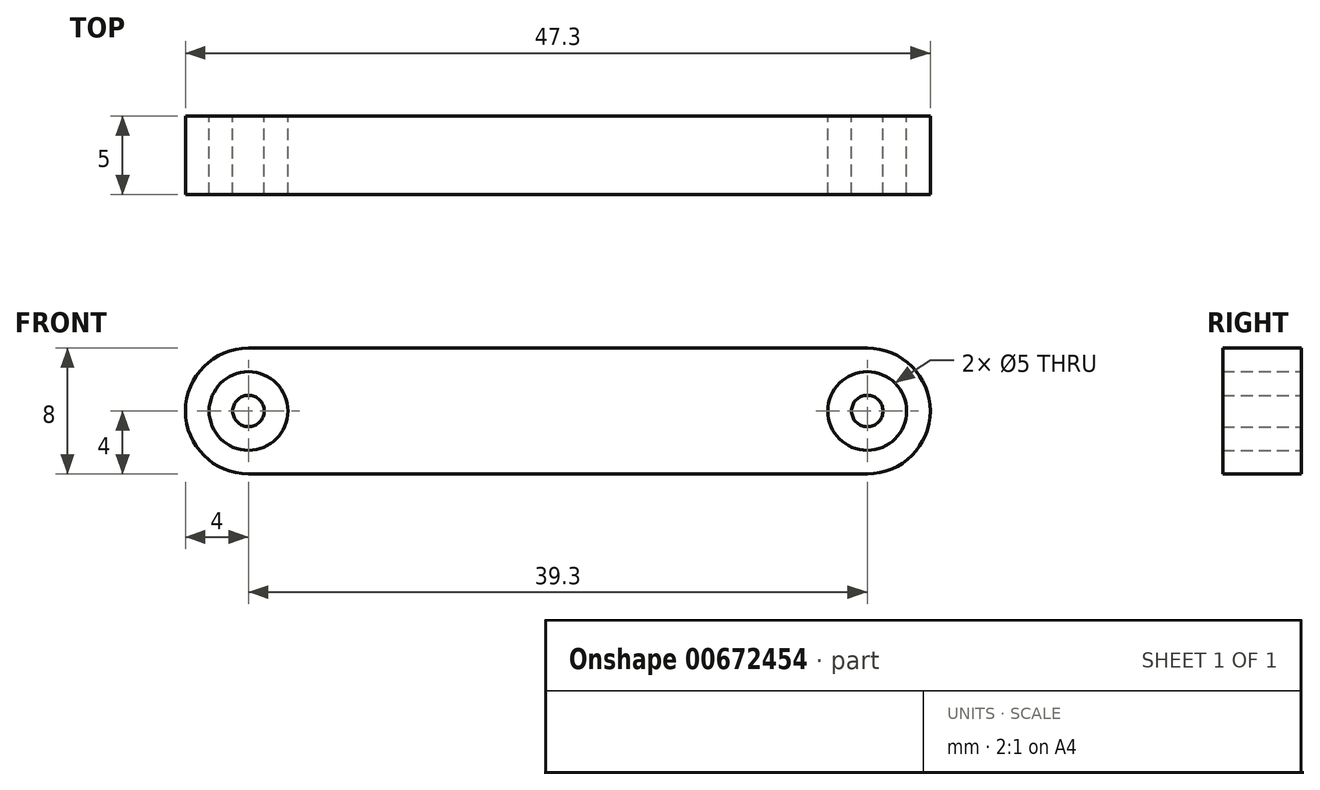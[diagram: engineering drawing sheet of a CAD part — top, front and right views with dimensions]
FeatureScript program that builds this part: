
annotation { "Feature Type Name" : "Feature", "Feature Type Description" : "" }
export const myFeature = defineFeature(function(context is Context, id is Id, definition is map)
    precondition{}
    {
        {
            var Q0;
            Q0=qCreatedBy(makeId("Front.planeOp"),FACE);
            var sketch = newSketch(context, id + "F0", { "sketchPlane" : qUnion([Q0])});
            skArc(sketch, "E0", {"start": v(0, 4) * mm, "mid": v(-4, 0) * mm, "end": v(0, -4) * mm});
            skCircle(sketch, "E1", {"center": v(0, 0) * mm, "radius": 2.5 * mm});
            skArc(sketch, "E2", {"start": v(39.3, -4) * mm, "mid": v(43.3, 0) * mm, "end": v(39.3, 4) * mm});
            skCircle(sketch, "E3", {"center": v(39.3, 0) * mm, "radius": 2.5 * mm});
            skLineSegment(sketch, "E4", {"start": v(0, 4) * mm, "end": v(39.3, 4) * mm});
            skLineSegment(sketch, "E5", {"start": v(0, -4) * mm, "end": v(39.3, -4) * mm});
            skCircle(sketch, "E6", {"center": v(0, 0) * mm, "radius": 1 * mm});
            skCircle(sketch, "E7", {"center": v(39.3, 0) * mm, "radius": 1 * mm});
            skSolve(sketch);
        }
        {
            var Q0;
            Q0=makeQuery(id+"F0.imprint","IMPRINT",FACE,{"disambiguationData":[TD([[makeQuery(id+"F0.imprint","IMPRINT",EDGE,{"derivedFrom":sQuery(id+"F0.wireOp",EDGE,"E0")}),1.0]])]});
            var Q1;
            Q1=makeQuery(id+"F0.imprint","IMPRINT",FACE,{"disambiguationData":[TD([[makeQuery(id+"F0.imprint","IMPRINT",EDGE,{"derivedFrom":sQuery(id+"F0.wireOp",EDGE,"E6")}),1.0]])]});
            var Q2;
            Q2=makeQuery(id+"F0.imprint","IMPRINT",FACE,{"disambiguationData":[TD([[makeQuery(id+"F0.imprint","IMPRINT",EDGE,{"derivedFrom":sQuery(id+"F0.wireOp",EDGE,"E7")}),1.0]])]});
            extrude(context, id + "F1", {"entities" : qUnion([Q0, Q1, Q2]), "endBound" : BoundingType.SYMMETRIC, "depth" : 5 * mm, "offsetDistance" : 25 * mm});
        }
    });
